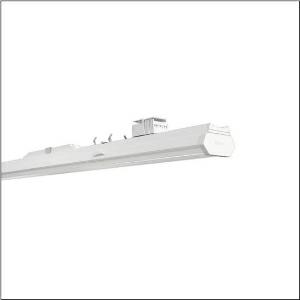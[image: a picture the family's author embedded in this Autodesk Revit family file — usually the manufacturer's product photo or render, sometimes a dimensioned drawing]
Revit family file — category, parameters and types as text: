
# Revit family: licross_11_protected_ho_51td11mn4gxs
name_source: partatom
category: Lighting Fixtures
units: mm (PartAtom-declared; Revit-internal decimal feet)

## family parameters
Cut with Voids When Loaded = No
Host = Face
Light Source = No
Part Type = Normal
Room Calculation Point = No
Round Connector Dimension = Use Diameter
Shared = No

## types (1)
- --- (1 x LED, 16070 lm, 87.4 W, 4000K)
    Apparent Load = 87 VA
    CIE Flux Codes = 84 94 98 99 100
    Color Rendering = 80
    Color Temperature = 4000K
    Default Elevation = 1800 mm
    Description = Licross 11 Protected HO, luminaire insert, of sheet steel, galvanised, coil coated, white, length: 1.500mm, width: 90mm, height: 101mm, LED rated luminous flux: 16.070lm, light colour: 840, SDCM (Standard Deviation of Colour Matching)MacAdam ≤ 2 SDCM (initial), control gear: ON/OFF Multilumen, with plug, 3-pole, with phase selection, mains connection: 220..240V, AC, 50/60Hz, rated input power: 87W, internal wiring halogen-free, primary light control with lens, of plastic, primary optical cover: cover, of PMMA, light emission: direct distribution, primary light characteristic: symmetric, protection rating (complete): IP54, insulation class (complete): insulation class I (protective earthing), certification: CE, ENEC, VDE, UKCA, protection symbol: D if used in an environment with non-conductive dust loads with corresponding accessories, impact resistance: IK06, permissible ambient temperature for indoor applications: -35..+35°C, corresponds to IFS (International Featured Standards) requirements for safety and quality in the food industry, reducing of maximum allowable ambient temperature of 5°C with ceiling mounting, LABS conformity tested according to VDMA 24364:2018-05, The light source and the operating device comply with the requirements of the Ecodesign Regulation (EU) 2019/2020 and are replaceable in accordance with this regulation, packaging unit: 1 piece
    Height = 92 mm
    Lamp = 1 x LED
    Lamp Light Flux = 16070 lm
    Lamp Power = 87.4 W
    Lamp count = 1
    Length = 1500 mm
    Luminous efficacy = 184 lm/W
    Manufacturer = Siteco
    ModVariant = No
    Model = 51TD11MN4GXS
    Mounting Place = Ceiling
    Mounting Type = Pendant
    Number of Poles = 1
    OnlyDefault = Yes
    Power Factor = 1
    Product Name = Licross 11 Protected HO
    Product group = luminaire insert | ceiling pendant
    ProductGroupID = 901
    Protection Class = Protection class I
    Protection Degree = IP 54
    RLX_Detail_Level = 1
    RLX_Emergency_Light_Flux = 0 lm
    RLX_Emergency_Type = 0
    RLX_Emergency_Type_DB = No
    RlxData = <blob elided: 22249 chars, md5=964424d8>
    Socket = socket
    Standby Power = 0 W
    System Light Flux = 16070 lm
    System Power = 87 W
    Type Comments = factory setting: luminous flux: 100 % | (A | C | E) | 203 mA
    Type Image = l_1256145.jpg
    URL = http://relux.com
    VarID = @adj_090437
    Voltage = 0 V
    Weight = 0.00 kg
    Width = 88 mm

## geometry (parser evidence)
native form markers: Blend x4, Sweep x11
no freeform markers — native parametric forms only
